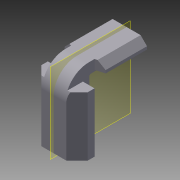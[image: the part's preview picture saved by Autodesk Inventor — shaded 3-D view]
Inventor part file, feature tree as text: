
AUTODESK INVENTOR PART (.ipt)
format: ipt  version: 2011 (Build 150239000, 239)  size: 105,472 bytes
history: native  units: in
note: dims shown in document units (in); Inventor stores cm internally (conversion verified against a paired STEP export)
features: imported_body x1, plane x1
ambient origin geometry x8: Origin, YZ Plane, XZ Plane, XY Plane, X Axis, Y Axis, Z Axis, Center Point
bodies: Solid1 (feature_tree)
feature tree (2):
  imported_body  "Base1"
  plane  "Work Plane1"
